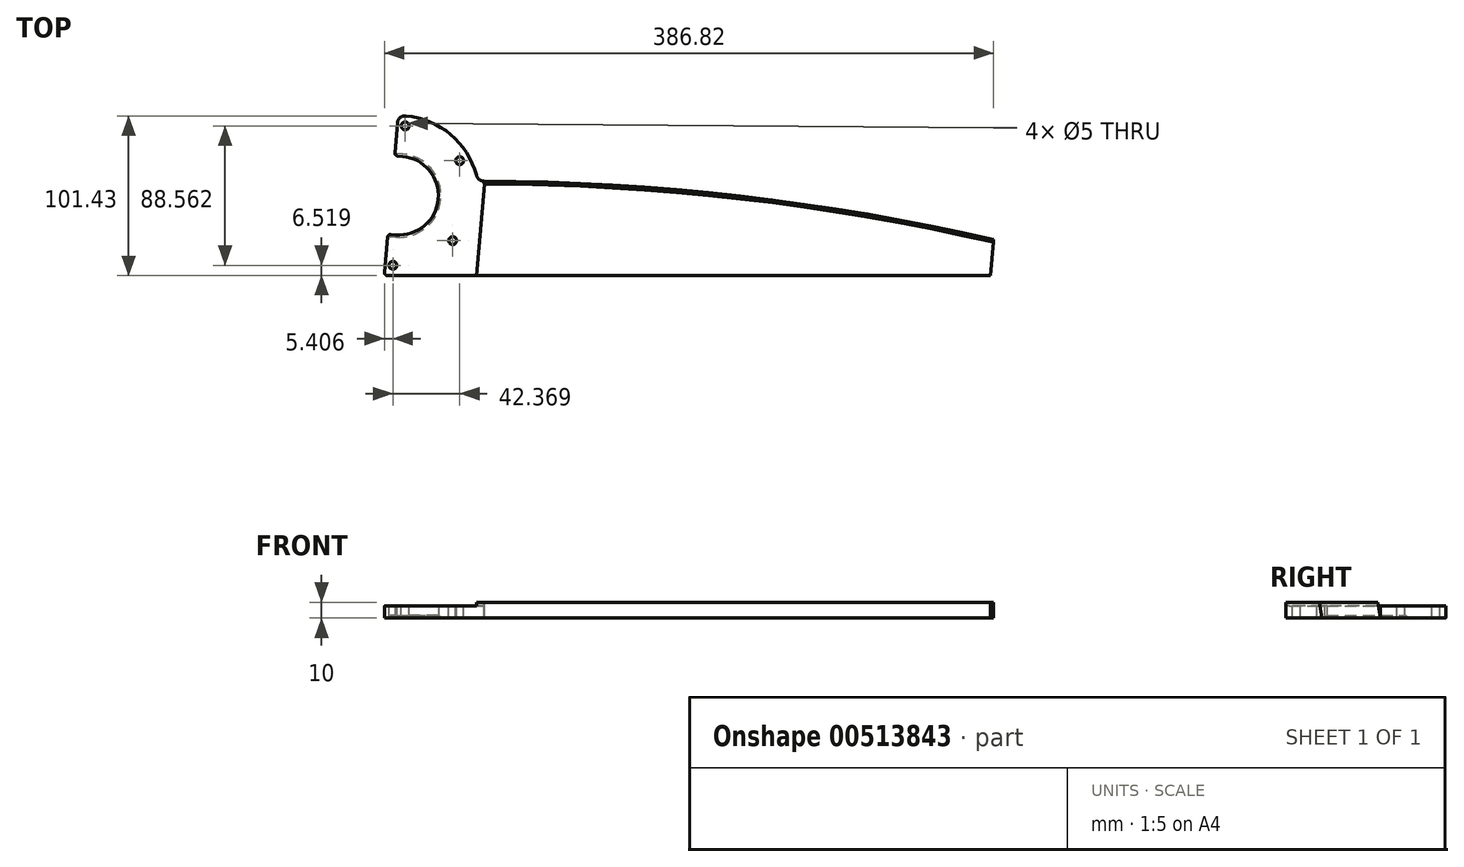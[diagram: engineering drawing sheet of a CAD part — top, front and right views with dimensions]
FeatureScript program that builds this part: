
annotation { "Feature Type Name" : "Feature", "Feature Type Description" : "" }
export const myFeature = defineFeature(function(context is Context, id is Id, definition is map)
    precondition{}
    {
        {
            var Q0;
            Q0=qCreatedBy(makeId("Top.planeOp"),FACE);
            var sketch = newSketch(context, id + "F0", { "sketchPlane" : qUnion([Q0])});
            skArc(sketch, "E0", {"start": v(-2.18, -24.9) * mm, "mid": v(24.9, -2.18) * mm, "end": v(2.18, 24.9) * mm});
            skLineSegment(sketch, "E1", {"start": v(-9.46, -50.8) * mm, "end": v(375.54, -50.8) * mm});
            skLineSegment(sketch, "E2", {"start": v(-9.46, -50.8) * mm, "end": v(-7.16, -24.47) * mm});
            skLineSegment(sketch, "E3", {"start": v(49.96, 9.2) * mm, "end": v(377.54, -27.89) * mm, "construction": true});
            skLineSegment(sketch, "E4", {"start": v(377.54, -27.89) * mm, "end": v(375.54, -50.8) * mm});
            skLineSegment(sketch, "E5", {"start": v(2.18, 24.9) * mm, "end": v(-2.8, 25.34) * mm});
            skLineSegment(sketch, "E6", {"start": v(-2.18, -24.9) * mm, "end": v(-7.16, -24.47) * mm});
            skLineSegment(sketch, "E7.trimOffspring", {"start": v(-2.8, 25.34) * mm, "end": v(-0.57, 50.8) * mm});
            skArc(sketch, "E8.trimOffspring", {"start": v(49.96, 9.2) * mm, "mid": v(32.28, 39.22) * mm, "end": v(-0.57, 50.8) * mm});
            skPoint(sketch, "E9.second.point", {"position": v(498.74, -41.8) * mm});
            skLineSegment(sketch, "E10", {"start": v(49.96, 9.2) * mm, "end": v(38.88, 9.2) * mm, "construction": true});
            skArc(sketch, "E11", {"start": v(49.96, 9.2) * mm, "mid": v(214.8, -0.1) * mm, "end": v(377.54, -27.89) * mm});
            skSolve(sketch);
        }
        {
            var Q0;
            {var subQ0=sQuery(id+"F0.wireOp",EDGE,"E0");Q0=makeQuery(id+"F0.imprint","IMPRINT",FACE,{"disambiguationData":[TD([[makeQuery(id+"F0.imprint","IMPRINT",EDGE,{"derivedFrom":subQ0}),-1.0]])]});}
            extrude(context, id + "F1", {"entities" : qUnion([Q0]), "depth" : 10 * mm});
        }
        {
            var Q0;
            Q0=makeQuery(id+"F1.opExtrude","SWEPT_EDGE",EDGE,{"disambiguationData":[OSD([sQuery(id+"F0.wireOp",EDGE,"E3"),sQuery(id+"F0.wireOp",EDGE,"E8.trimOffspring")])]});
            fillet(context, id + "F2", {"entities" : qUnion([Q0]), "radius" : 5 * mm, "tangentPropagation" : true, "allowEdgeOverflow" : false});
        }
        {
            var Q0;
            Q0=makeQuery(id+"F1.opExtrude","SWEPT_EDGE",EDGE,{"disambiguationData":[OSD([sQuery(id+"F0.wireOp",EDGE,"E5"),sQuery(id+"F0.wireOp",EDGE,"E7.trimOffspring")])]});
            var Q1;
            Q1=makeQuery(id+"F1.opExtrude","SWEPT_EDGE",EDGE,{"disambiguationData":[OSD([sQuery(id+"F0.wireOp",EDGE,"E7.trimOffspring"),sQuery(id+"F0.wireOp",EDGE,"E8.trimOffspring")])]});
            var Q2;
            Q2=makeQuery(id+"F1.opExtrude","SWEPT_EDGE",EDGE,{"disambiguationData":[OSD([sQuery(id+"F0.wireOp",EDGE,"E1"),sQuery(id+"F0.wireOp",EDGE,"E2")])]});
            var Q3;
            Q3=makeQuery(id+"F1.opExtrude","SWEPT_EDGE",EDGE,{"disambiguationData":[OSD([sQuery(id+"F0.wireOp",EDGE,"E2"),sQuery(id+"F0.wireOp",EDGE,"E6")])]});
            fillet(context, id + "F3", {"entities" : qUnion([Q0, Q1, Q2, Q3]), "radius" : 2 * mm, "tangentPropagation" : true, "allowEdgeOverflow" : false});
        }
        {
            var Q0;
            Q0=makeQuery(id+"F1.opExtrude","CAP_FACE",FACE,{"disambiguationData":[OSD([sQuery(id+"F0.wireOp",EDGE,"E0"),sQuery(id+"F0.wireOp",EDGE,"E1"),sQuery(id+"F0.wireOp",EDGE,"E2"),sQuery(id+"F0.wireOp",EDGE,"E4"),sQuery(id+"F0.wireOp",EDGE,"E5"),sQuery(id+"F0.wireOp",EDGE,"E6"),sQuery(id+"F0.wireOp",EDGE,"E7.trimOffspring"),sQuery(id+"F0.wireOp",EDGE,"E8.trimOffspring"),sQuery(id+"F0.wireOp",EDGE,"E11")])],"isStart":false});
            var sketch = newSketch(context, id + "F4", { "sketchPlane" : qUnion([Q0])});
            skCircle(sketch, "E12", {"center": v(0, 0) * mm, "radius": 44.45 * mm, "construction": true});
            skLineSegment(sketch, "E13", {"start": v(0, 0) * mm, "end": v(3.87, 44.28) * mm, "construction": true});
            skLineSegment(sketch, "E14", {"start": v(0, 0) * mm, "end": v(38.5, 22.23) * mm, "construction": true});
            skLineSegment(sketch, "E15", {"start": v(0, 0) * mm, "end": v(34.05, -28.57) * mm, "construction": true});
            skLineSegment(sketch, "E16", {"start": v(0, 0) * mm, "end": v(-3.87, -44.28) * mm, "construction": true});
            skPoint(sketch, "E17", {"position": v(3.87, 44.28) * mm});
            skPoint(sketch, "E18", {"position": v(38.5, 22.23) * mm});
            skPoint(sketch, "E19", {"position": v(34.05, -28.57) * mm});
            skPoint(sketch, "E20", {"position": v(-3.87, -44.28) * mm});
            skSolve(sketch);
        }
        {
            var Q0;
            Q0=sQuery(id+"F4.wireOp",VERTEX,"E20");
            var Q1;
            Q1=sQuery(id+"F4.wireOp",VERTEX,"E15.end");
            var Q2;
            Q2=sQuery(id+"F4.wireOp",VERTEX,"E18");
            var Q3;
            Q3=sQuery(id+"F4.wireOp",VERTEX,"E17");
            var Q4;
            Q4=makeQuery(id+"F1.opExtrude","SWEPT_BODY",BODY,{"disambiguationData":[OSD([sQuery(id+"F0.wireOp",EDGE,"E0"),sQuery(id+"F0.wireOp",EDGE,"E1"),sQuery(id+"F0.wireOp",EDGE,"E2"),sQuery(id+"F0.wireOp",EDGE,"E4"),sQuery(id+"F0.wireOp",EDGE,"E5"),sQuery(id+"F0.wireOp",EDGE,"E6"),sQuery(id+"F0.wireOp",EDGE,"E7.trimOffspring"),sQuery(id+"F0.wireOp",EDGE,"E8.trimOffspring"),sQuery(id+"F0.wireOp",EDGE,"E11")])]});
            hole(context, id + "F5", {"style" : HoleStyle.SIMPLE, "endStyle" : HoleEndStyle.THROUGH, "standardTappedOrClearance" : lookupTablePath({ "standard" : "ISO", "engagement" : "75%", "pitch" : "1 mm", "size" : "M6", "type" : "Tapped" }), "standardBlindInLast" : lookupTablePath({ "standard" : "ISO", "engagement" : "75%", "pitch" : "1 mm", "size" : "M6", "type" : "Tapped" }), "holeDiameter" : 5 * mm, "showTappedDepth" : true, "isTappedThrough" : true, "tappedDepth" : 12 * mm, "tapClearance" : 3, "locations" : qUnion([Q0, Q1, Q2, Q3]), "scope" : qUnion([Q4]), "majorDiameter" : 6 * mm});
        }
        {
            var Q0;
            Q0=makeQuery(id+"F1.opExtrude","SWEPT_FACE",FACE,{"disambiguationData":[OSD([sQuery(id+"F0.wireOp",EDGE,"E4")])]});
            var sketch = newSketch(context, id + "F6", { "sketchPlane" : qUnion([Q0])});
            skLineSegment(sketch, "E21", {"start": v(5.12, 0) * mm, "end": v(3.36, 10) * mm});
            skSolve(sketch);
        }
        {
            var Q0;
            {var subQ0=sQuery(id+"F6.wireOp",EDGE,"E21");Q0=makeQuery(id+"F6.imprint","IMPRINT",FACE,{"disambiguationData":[TD([[makeQuery(id+"F6.imprint","IMPRINT",EDGE,{"derivedFrom":subQ0}),-1.0]])]});}
            var Q1;
            Q1=makeQuery(id+"F1.opExtrude","CAP_EDGE",EDGE,{"disambiguationData":[OSD([sQuery(id+"F0.wireOp",EDGE,"E11")])],"isStart":false});
            sweep(context, id + "F7", {"operationType" : NewBodyOperationType.REMOVE, "profiles" : qUnion([Q0]), "path" : qUnion([Q1])});
        }
        {
            var Q0;
            Q0=makeQuery(id+"F1.opExtrude","CAP_FACE",FACE,{"disambiguationData":[OSD([sQuery(id+"F0.wireOp",EDGE,"E0"),sQuery(id+"F0.wireOp",EDGE,"E1"),sQuery(id+"F0.wireOp",EDGE,"E2"),sQuery(id+"F0.wireOp",EDGE,"E4"),sQuery(id+"F0.wireOp",EDGE,"E5"),sQuery(id+"F0.wireOp",EDGE,"E6"),sQuery(id+"F0.wireOp",EDGE,"E7.trimOffspring"),sQuery(id+"F0.wireOp",EDGE,"E8.trimOffspring"),sQuery(id+"F0.wireOp",EDGE,"E11")])],"isStart":false});
            var sketch = newSketch(context, id + "F8", { "sketchPlane" : qUnion([Q0])});
            skLineSegment(sketch, "E22", {"start": v(54.19, 7.45) * mm, "end": v(49.1, -50.8) * mm});
            skSolve(sketch);
        }
        {
            var Q0;
            {var subQ12=sQuery(id+"F8.wireOp",EDGE,"E22");Q0=makeQuery(id+"F8.imprint","IMPRINT",FACE,{"disambiguationData":[TD([[makeQuery(id+"F8.imprint","IMPRINT",EDGE,{"derivedFrom":subQ12}),-1.0]])]});}
            extrude(context, id + "F9", {"entities" : qUnion([Q0]), "operationType" : NewBodyOperationType.REMOVE, "oppositeDirection" : true, "depth" : (10 - 7.6) * mm});
        }
        {
            var Q0;
            Q0=makeQuery(id+"F9.boolean.opBoolean","COPY",EDGE,{"derivedFrom":makeQuery(id+"F9.opExtrude","CAP_EDGE",EDGE,{"disambiguationData":[OSD([sQuery(id+"F0.wireOp",EDGE,"E0")])],"isStart":false})});
            var Q1;
            Q1=makeQuery(id+"F9.boolean.opBoolean","COPY",EDGE,{"derivedFrom":makeQuery(id+"F9.opExtrude","CAP_EDGE",EDGE,{"disambiguationData":[OSD([sQuery(id+"F0.wireOp",EDGE,"E5")])],"isStart":false})});
            var Q2;
            Q2=makeQuery(id+"F9.boolean.opBoolean","COPY",EDGE,{"derivedFrom":makeQuery(id+"F9.opExtrude","CAP_EDGE",EDGE,{"disambiguationData":[OSD([sQuery(id+"F0.wireOp",EDGE,"E6")])],"isStart":false})});
            var Q3;
            Q3=makeQuery(id+"F1.opExtrude","CAP_EDGE",EDGE,{"disambiguationData":[OSD([sQuery(id+"F0.wireOp",EDGE,"E0")])],"isStart":true});
            var Q4;
            Q4=makeQuery(id+"F1.opExtrude","CAP_EDGE",EDGE,{"disambiguationData":[OSD([sQuery(id+"F0.wireOp",EDGE,"E5")])],"isStart":true});
            var Q5;
            Q5=makeQuery(id+"F1.opExtrude","CAP_EDGE",EDGE,{"disambiguationData":[OSD([sQuery(id+"F0.wireOp",EDGE,"E6")])],"isStart":true});
            chamfer(context, id + "F10", {"entities" : qUnion([Q0, Q1, Q2, Q3, Q4, Q5]), "width" : 1.5 * mm});
        }
    });
